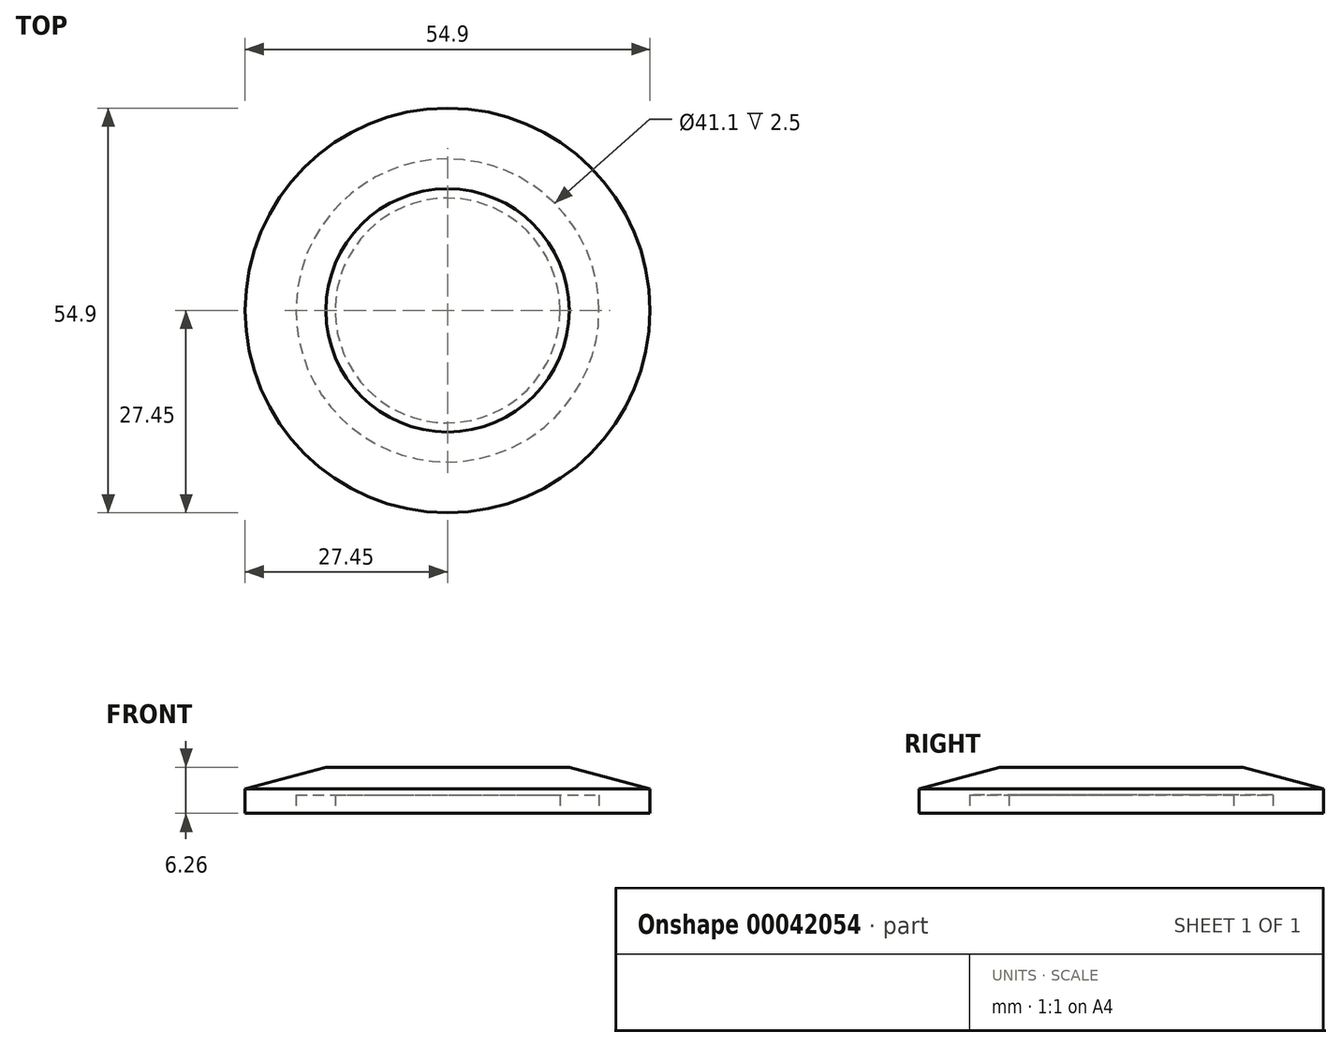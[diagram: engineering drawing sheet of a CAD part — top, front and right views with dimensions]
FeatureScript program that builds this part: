
annotation { "Feature Type Name" : "Feature", "Feature Type Description" : "" }
export const myFeature = defineFeature(function(context is Context, id is Id, definition is map)
    precondition{}
    {
        {
            var Q0;
            Q0=qCreatedBy(makeId("Front.planeOp"),FACE);
            var sketch = newSketch(context, id + "F0", { "sketchPlane" : qUnion([Q0])});
            skLineSegment(sketch, "E0", {"start": v(0, 0) * mm, "end": v(0, 6.26) * mm});
            skLineSegment(sketch, "E1", {"start": v(0, 6.26) * mm, "end": v(16.5, 6.26) * mm});
            skLineSegment(sketch, "E2", {"start": v(16.5, 6.26) * mm, "end": v(27.45, 3.3) * mm});
            skLineSegment(sketch, "E3", {"start": v(27.45, 3.3) * mm, "end": v(27.45, 0) * mm});
            skLineSegment(sketch, "E4", {"start": v(27.45, 0) * mm, "end": v(20.55, 0) * mm});
            skLineSegment(sketch, "E5", {"start": v(15.25, 0) * mm, "end": v(15.25, 2.5) * mm});
            skLineSegment(sketch, "E6", {"start": v(15.25, 2.5) * mm, "end": v(20.55, 2.5) * mm});
            skLineSegment(sketch, "E7", {"start": v(20.55, 2.5) * mm, "end": v(20.55, 0) * mm});
            skLineSegment(sketch, "E8.trimOffspring", {"start": v(15.25, 0) * mm, "end": v(0, 0) * mm});
            skSolve(sketch);
        }
        {
            var Q0;
            Q0=makeQuery(id+"F0.imprint","IMPRINT",FACE,{"disambiguationData":[TD([[makeQuery(id+"F0.imprint","IMPRINT",EDGE,{"derivedFrom":sQuery(id+"F0.wireOp",EDGE,"E0")}),-1.0]])]});
            var Q1;
            Q1=sQuery(id+"F0.wireOp",EDGE,"E0");
            revolve(context, id + "F1", {"entities" : qUnion([Q0]), "axis" : qUnion([Q1]), "revolveType" : RevolveType.FULL});
        }
    });
